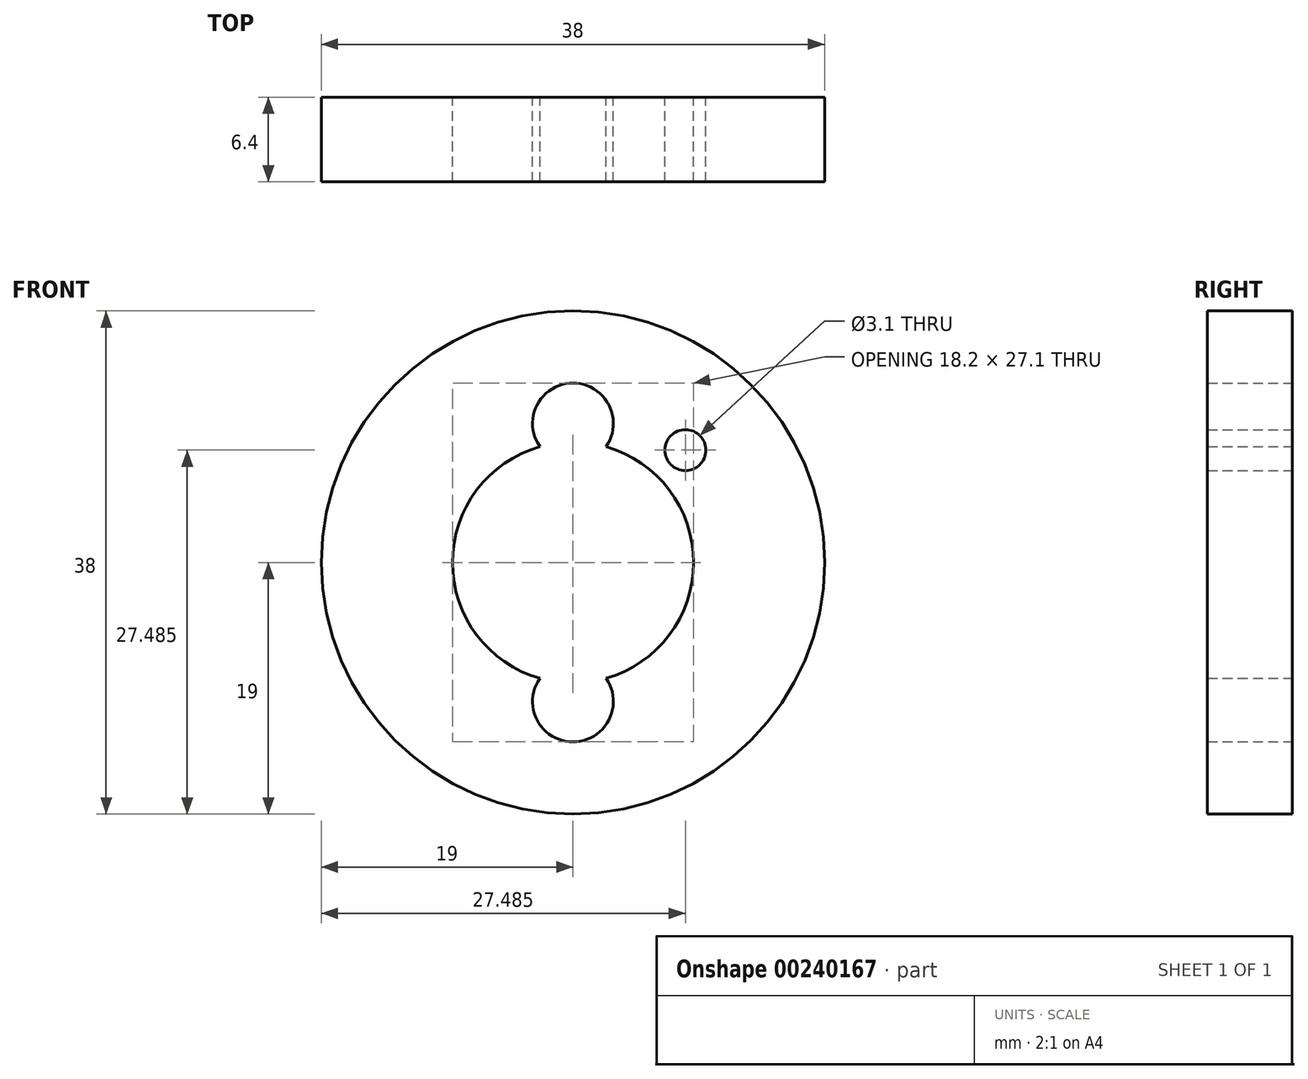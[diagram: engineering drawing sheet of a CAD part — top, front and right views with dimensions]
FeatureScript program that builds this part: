
annotation { "Feature Type Name" : "Feature", "Feature Type Description" : "" }
export const myFeature = defineFeature(function(context is Context, id is Id, definition is map)
    precondition{}
    {
        {
            var Q0;
            Q0=qCreatedBy(makeId("Front.planeOp"),FACE);
            var sketch = newSketch(context, id + "F0", { "sketchPlane" : qUnion([Q0])});
            skCircle(sketch, "E0", {"center": v(0, 0) * mm, "radius": 19 * mm});
            skSolve(sketch);
        }
        {
            var Q0;
            Q0=makeQuery(id+"F0.imprint","IMPRINT",FACE,{"disambiguationData":[TD([[makeQuery(id+"F0.imprint","IMPRINT",EDGE,{"derivedFrom":sQuery(id+"F0.wireOp",EDGE,"E0")}),1.0]])]});
            extrude(context, id + "F1", {"entities" : qUnion([Q0]), "depth" : 6.4 * mm});
        }
        {
            var Q0;
            Q0=qCreatedBy(makeId("Front.planeOp"),FACE);
            var sketch = newSketch(context, id + "F2", { "sketchPlane" : qUnion([Q0])});
            skLineSegment(sketch, "E1", {"start": v(0, 0) * mm, "end": v(18.26, 18.26) * mm, "construction": true});
            skCircle(sketch, "E2", {"center": v(0, 0) * mm, "radius": 12 * mm, "construction": true});
            skCircle(sketch, "E3", {"center": v(8.49, 8.49) * mm, "radius": 1.55 * mm});
            skSolve(sketch);
        }
        {
            var Q0;
            Q0=qSketchRegion(id+"F2",true);
            extrude(context, id + "F3", {"entities" : qUnion([Q0]), "operationType" : NewBodyOperationType.REMOVE, "depth" : 25.4 * mm});
        }
        {
            var Q0;
            Q0=qCreatedBy(makeId("Front.planeOp"),FACE);
            var sketch = newSketch(context, id + "F4", { "sketchPlane" : qUnion([Q0])});
            skCircle(sketch, "E4", {"center": v(0, 0) * mm, "radius": 9.1 * mm});
            skSolve(sketch);
        }
        {
            var Q0;
            Q0=qSketchRegion(id+"F4",true);
            extrude(context, id + "F5", {"entities" : qUnion([Q0]), "operationType" : NewBodyOperationType.REMOVE, "endBound" : BoundingType.THROUGH_ALL, "depth" : 25.4 * mm});
        }
        {
            var Q0;
            Q0=qCreatedBy(makeId("Front.planeOp"),FACE);
            var sketch = newSketch(context, id + "F6", { "sketchPlane" : qUnion([Q0])});
            skCircle(sketch, "E5", {"center": v(0, 0) * mm, "radius": 10.5 * mm, "construction": true});
            skCircle(sketch, "E6", {"center": v(0, 10.5) * mm, "radius": 3.05 * mm});
            skCircle(sketch, "E7", {"center": v(0, -10.5) * mm, "radius": 3.05 * mm});
            skSolve(sketch);
        }
        {
            var Q0;
            Q0 = qSketchRegion(id + "F6", true);
            extrude(context, id + "F7", {"entities" : qUnion([Q0]), "operationType" : NewBodyOperationType.REMOVE, "endBound" : BoundingType.THROUGH_ALL, "depth" : 25 * mm});
        }
    });
